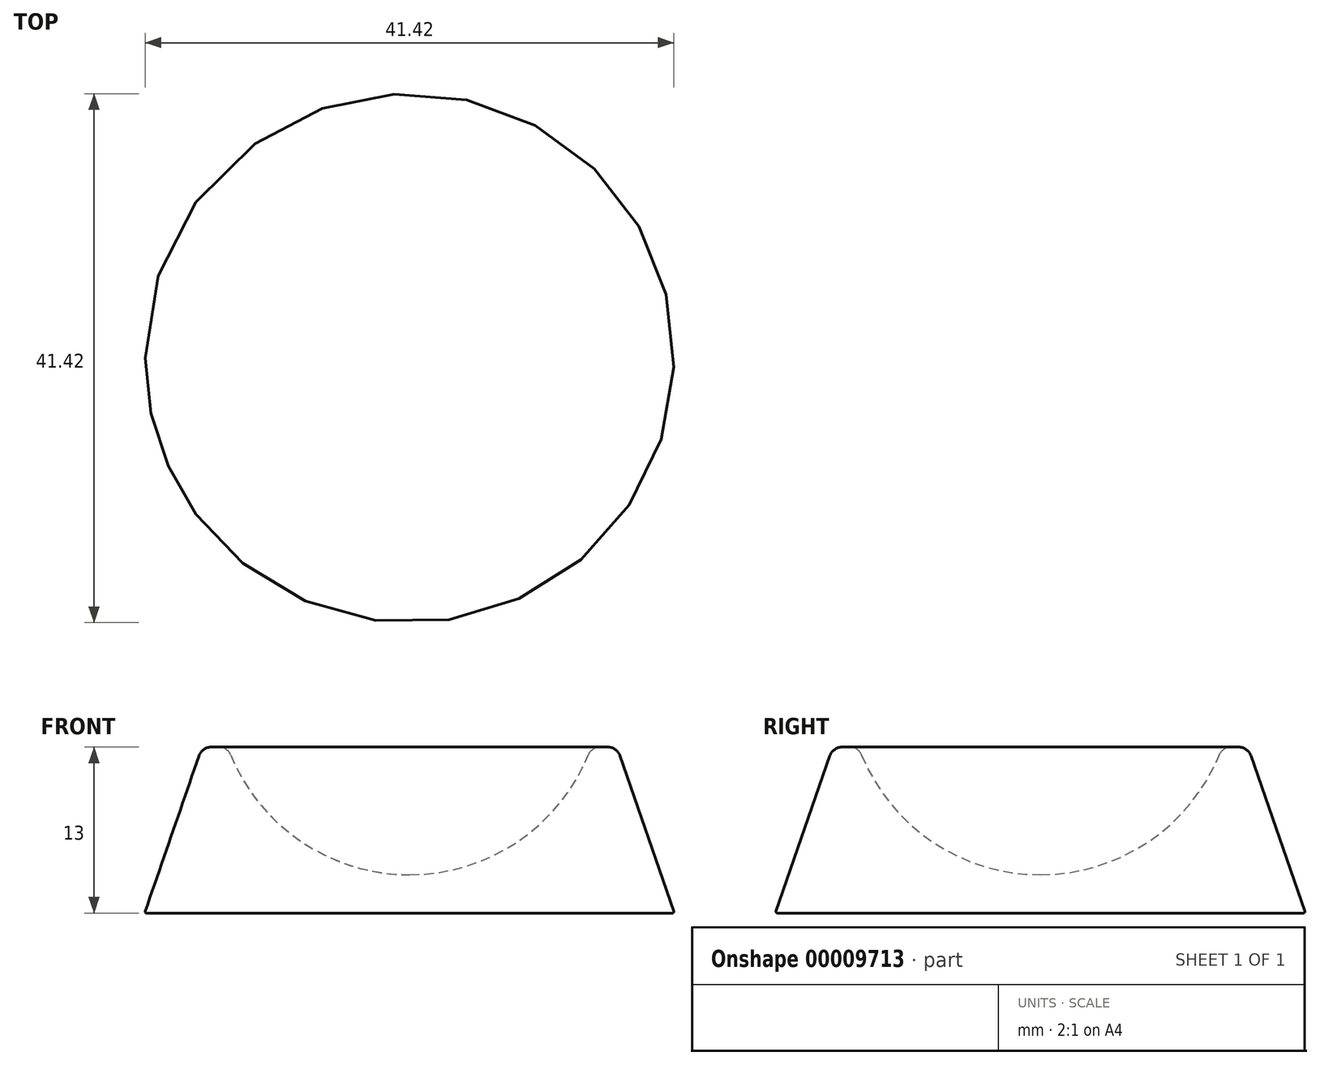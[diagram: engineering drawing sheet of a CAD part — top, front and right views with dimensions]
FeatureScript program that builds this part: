
annotation { "Feature Type Name" : "Feature", "Feature Type Description" : "" }
export const myFeature = defineFeature(function(context is Context, id is Id, definition is map)
    precondition{}
    {
        {
            var Q0;
            Q0=qCreatedBy(makeId("Front.planeOp"),FACE);
            var sketch = newSketch(context, id + "F0", { "sketchPlane" : qUnion([Q0])});
            skLineSegment(sketch, "E0", {"start": v(0, 0) * mm, "end": v(-20.75, 0) * mm});
            skLineSegment(sketch, "E1", {"start": v(-20.75, 0) * mm, "end": v(-16.25, 13) * mm});
            skLineSegment(sketch, "E2", {"start": v(0, 0) * mm, "end": v(0, 3) * mm});
            skLineSegment(sketch, "E3", {"start": v(-14.25, 13) * mm, "end": v(-16.25, 13) * mm});
            skArc(sketch, "E4", {"start": v(-14.25, 13) * mm, "mid": v(-8.7, 5.75) * mm, "end": v(0, 3) * mm});
            skSolve(sketch);
        }
        {
            var Q0;
            Q0 = qSketchRegion(id + "F0", true);
            var Q1;
            Q1=sQuery(id+"F0.wireOp",EDGE,"E2");
            revolve(context, id + "F1", {"entities" : qUnion([Q0]), "axis" : qUnion([Q1]), "revolveType" : RevolveType.FULL});
        }
        {
            var Q0;
            Q0=makeQuery(id+"F1.opRevolve","SWEPT_EDGE",EDGE,{"disambiguationData":[OSD([sQuery(id+"F0.wireOp",EDGE,"E1"),sQuery(id+"F0.wireOp",EDGE,"E3")])]});
            var Q1;
            Q1=makeQuery(id+"F1.opRevolve","SWEPT_EDGE",EDGE,{"disambiguationData":[OSD([sQuery(id+"F0.wireOp",EDGE,"E3"),sQuery(id+"F0.wireOp",EDGE,"E4")])]});
            fillet(context, id + "F2", {"entities" : qUnion([Q0, Q1]), "radius" : 1 * mm, "tangentPropagation" : true, "allowEdgeOverflow" : false});
        }
        {
            var Q0;
            Q0=makeQuery(id+"F1.opRevolve","SWEPT_EDGE",EDGE,{"disambiguationData":[OSD([sQuery(id+"F0.wireOp",EDGE,"E0"),sQuery(id+"F0.wireOp",EDGE,"E1")])]});
            fillet(context, id + "F3", {"entities" : qUnion([Q0]), "radius" : .1 * mm, "tangentPropagation" : true, "allowEdgeOverflow" : false});
        }
    });
